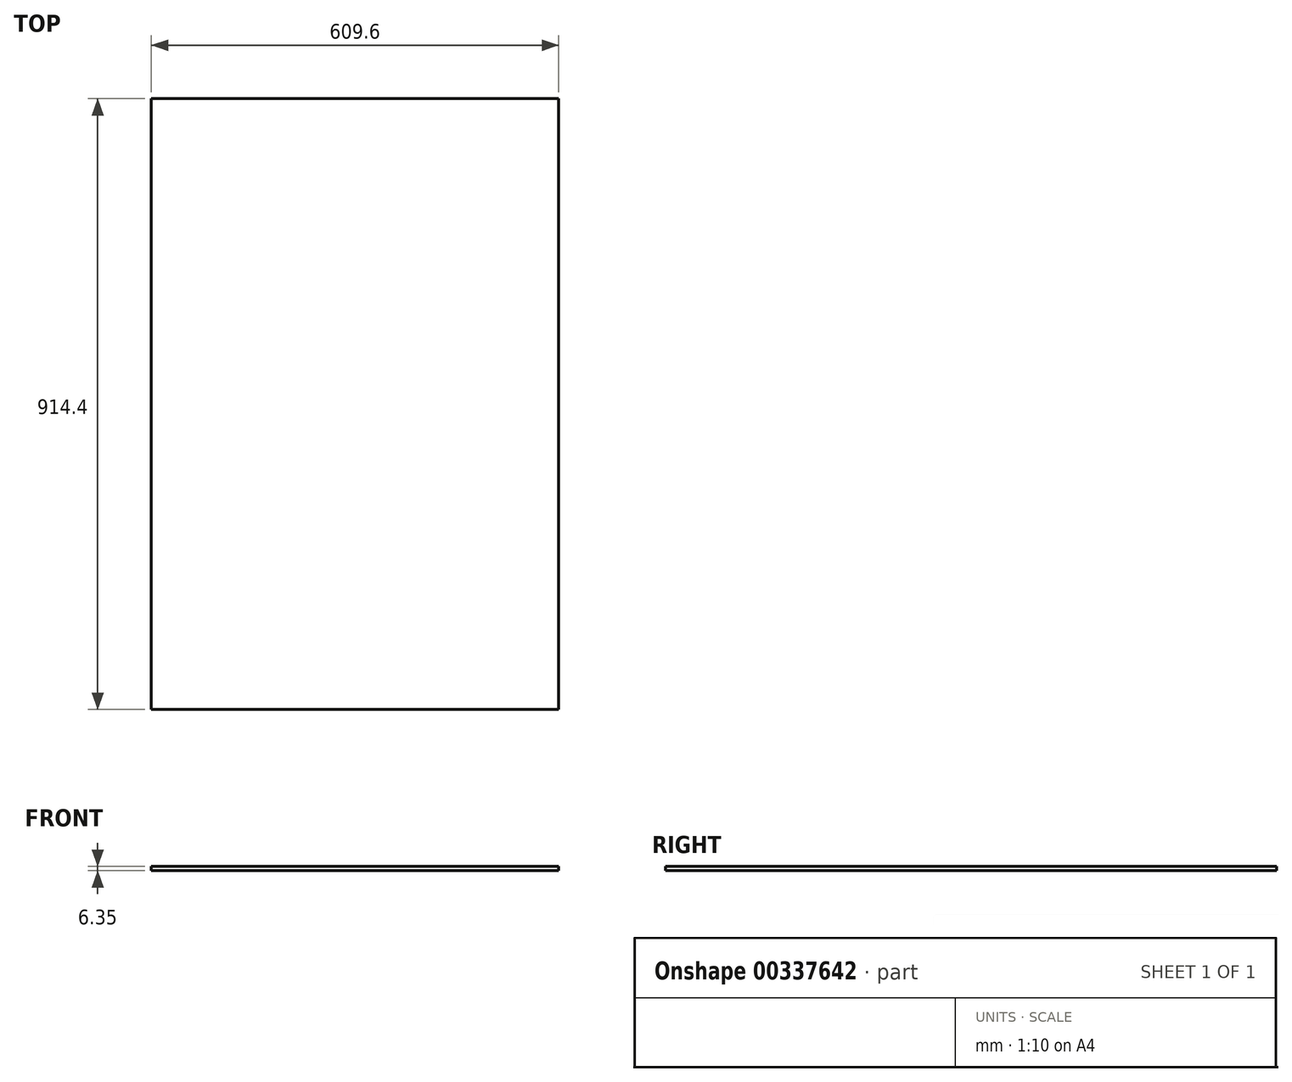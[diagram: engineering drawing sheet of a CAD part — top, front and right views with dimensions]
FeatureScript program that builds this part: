
annotation { "Feature Type Name" : "Feature", "Feature Type Description" : "" }
export const myFeature = defineFeature(function(context is Context, id is Id, definition is map)
    precondition{}
    {
        {
            var Q0;
            Q0=qCreatedBy(makeId("Top.planeOp"),FACE);
            var sketch = newSketch(context, id + "F0", { "sketchPlane" : qUnion([Q0])});
            skLineSegment(sketch, "E0", {"start": v(0, 0) * mm, "end": v(0, 533.4) * mm, "construction": true});
            skLineSegment(sketch, "E1", {"start": v(0, 533.4) * mm, "end": v(-304.8, 533.4) * mm});
            skLineSegment(sketch, "E2", {"start": v(-304.8, 533.4) * mm, "end": v(-304.8, 0) * mm});
            skLineSegment(sketch, "E3", {"start": v(-304.8, 0) * mm, "end": v(0, 0) * mm, "construction": true});
            skLineSegment(sketch, "E4", {"start": v(-304.8, -381) * mm, "end": v(-304.8, 0) * mm});
            skLineSegment(sketch, "E5", {"start": v(-304.8, -381) * mm, "end": v(0, -381) * mm});
            skLineSegment(sketch, "E6.MirrorCS", {"start": v(0, 533.4) * mm, "end": v(304.8, 533.4) * mm});
            skLineSegment(sketch, "E7.MirrorCS", {"start": v(304.8, 533.4) * mm, "end": v(304.8, 0) * mm});
            skLineSegment(sketch, "E8.MirrorCS", {"start": v(304.8, -381) * mm, "end": v(304.8, 0) * mm});
            skLineSegment(sketch, "E9.MirrorCS", {"start": v(304.8, -381) * mm, "end": v(0, -381) * mm});
            skSolve(sketch);
        }
        {
            var Q0;
            Q0 = qSketchRegion(id + "F0", true);
            extrude(context, id + "F1", {"entities" : qUnion([Q0]), "depth" : 6.35 * mm});
        }
    });
